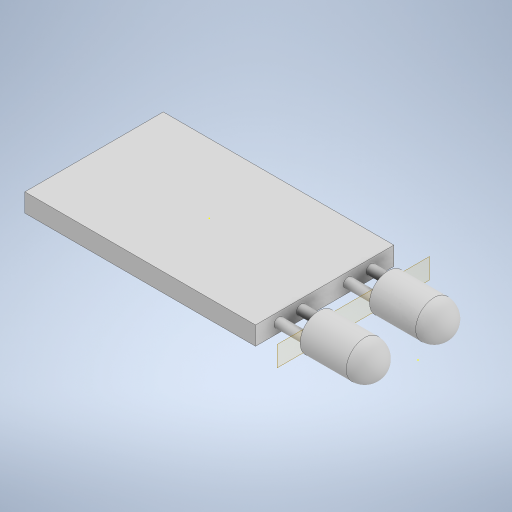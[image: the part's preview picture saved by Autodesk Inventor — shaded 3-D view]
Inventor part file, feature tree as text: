
AUTODESK INVENTOR PART (.ipt)
format: ipt  version: 2023 (Build 270158000, 158)  size: 262,144 bytes
history: native  units: in
note: dims shown in document units (in); Inventor stores cm internally (conversion verified against a paired STEP export)
features: sketch x5, extrude x3, fillet x2, plane x1
ambient origin geometry x8: Origin, YZ Plane, XZ Plane, XY Plane, X Axis, Y Axis, Z Axis, Center Point
bodies: Solid1 (feature_tree)
feature tree (11):
  extrude  "Extrusion1"  Depth=0.5906in
  extrude  "Extrusion2"  Depth=0.0787in
  plane  "Work Plane1"
  extrude  "Extrusion3"  Depth=0.1181in
  sketch  "Sketch5"  dims[d10=0.122in]
  fillet  "Fillet1"  Radius=0.0394in
  fillet  "Fillet2"  Radius=0.1181in
  sketch  "Sketch6"  dims[d11=0.1575in d12=0.1575in d13=0.2756in d14=0.0in d15=0.0787in d16=0.0787in]
  sketch  "Sketch1"  dims[d0=0.9843in d1=0.5906in]
  sketch  "Sketch2"  dims[d2=0.0787in d3=0.0in d4=0.0394in]
  sketch  "Sketch4"  dims[d5=0.0394in d6=0.0394in d7=0.0394in d8=0.1181in d9=0.0in]
